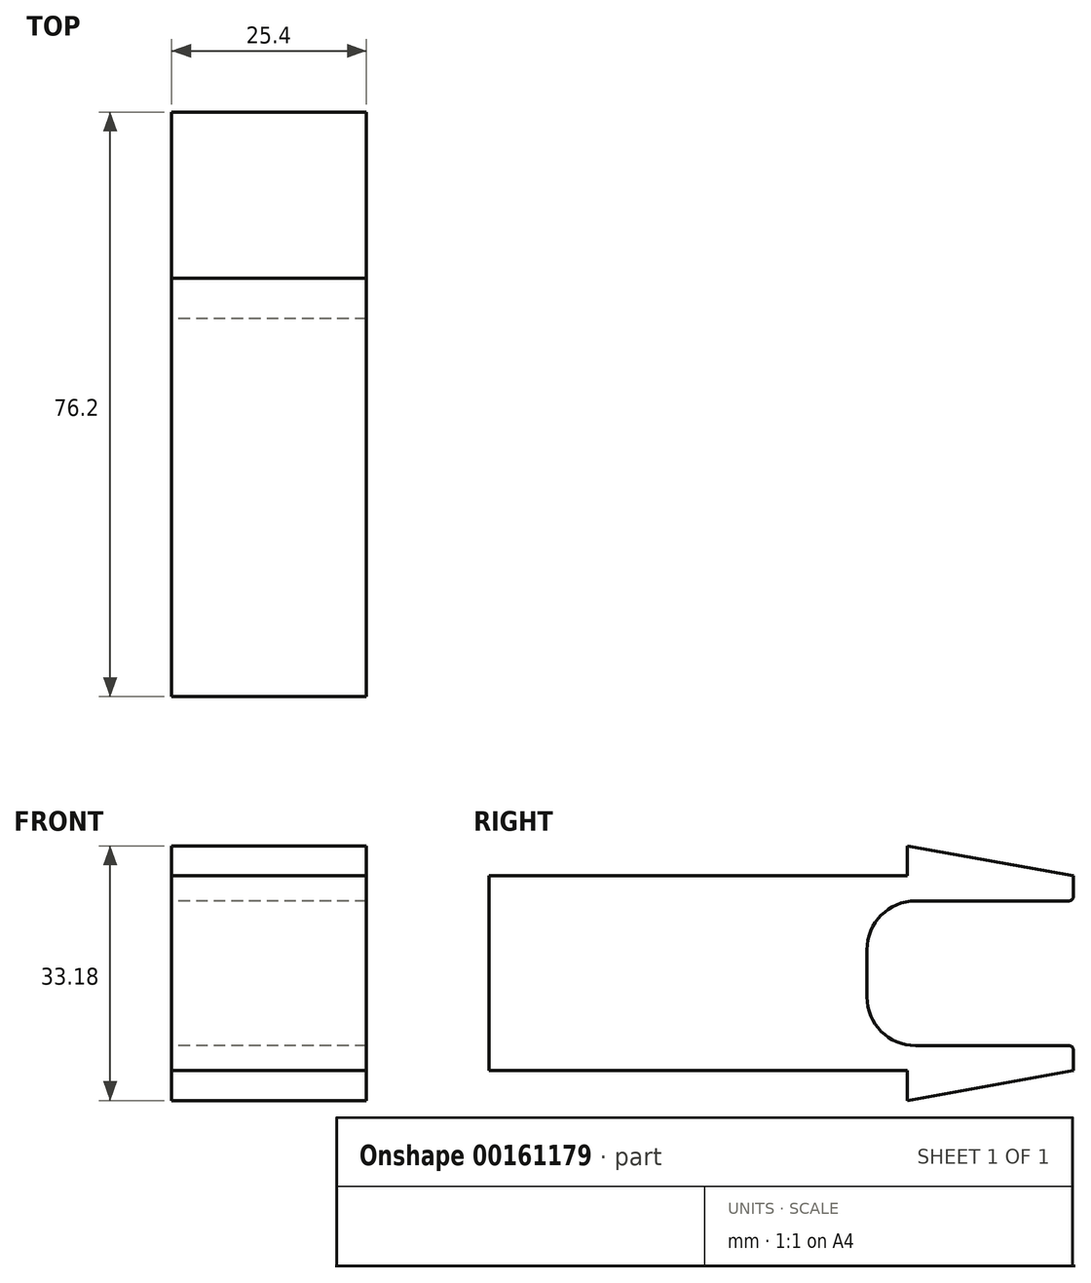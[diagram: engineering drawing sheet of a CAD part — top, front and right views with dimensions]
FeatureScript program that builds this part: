
annotation { "Feature Type Name" : "Feature", "Feature Type Description" : "" }
export const myFeature = defineFeature(function(context is Context, id is Id, definition is map)
    precondition{}
    {
        {
            var Q0;
            Q0=qCreatedBy(makeId("Right.planeOp"),FACE);
            var sketch = newSketch(context, id + "F0", { "sketchPlane" : qUnion([Q0])});
            skLineSegment(sketch, "E0.bottom", {"start": v(-38.1, 12.7) * mm, "end": v(38.1, 12.7) * mm});
            skLineSegment(sketch, "E0.top", {"start": v(-38.1, -12.7) * mm, "end": v(38.1, -12.7) * mm});
            skLineSegment(sketch, "E0.left", {"start": v(-38.1, 12.7) * mm, "end": v(-38.1, -12.7) * mm});
            skLineSegment(sketch, "E0.right", {"start": v(38.1, 12.7) * mm, "end": v(38.1, 10.06) * mm});
            skPoint(sketch, "E1", {"position": v(0, 12.7) * mm});
            skPoint(sketch, "E2", {"position": v(0, -12.7) * mm});
            skPoint(sketch, "E3", {"position": v(38.1, 0) * mm});
            skPoint(sketch, "E3.positionSnap0", {"position": v(38.1, 0) * mm});
            skPoint(sketch, "E4", {"position": v(-38.1, 0) * mm});
            skLineSegment(sketch, "E5", {"start": v(16.45, 12.7) * mm, "end": v(16.45, 16.59) * mm});
            skLineSegment(sketch, "E6", {"start": v(16.45, 16.59) * mm, "end": v(38.1, 12.7) * mm});
            skLineSegment(sketch, "E7", {"start": v(16.45, -12.7) * mm, "end": v(16.45, -16.59) * mm});
            skLineSegment(sketch, "E8", {"start": v(16.45, -16.59) * mm, "end": v(38.1, -12.7) * mm});
            skLineSegment(sketch, "E9.bottom", {"start": v(17.52, 9.43) * mm, "end": v(37.46, 9.43) * mm});
            skLineSegment(sketch, "E9.top", {"start": v(17.52, -9.43) * mm, "end": v(37.46, -9.43) * mm});
            skLineSegment(sketch, "E9.left", {"start": v(11.17, 3.08) * mm, "end": v(11.17, -3.08) * mm});
            skLineSegment(sketch, "E9.right", {"start": v(38.1, 9.43) * mm, "end": v(38.1, -9.43) * mm});
            skPoint(sketch, "E10", {"position": v(11.17, 0) * mm});
            skPoint(sketch, "E11.visualSharp", {"position": v(11.17, 9.43) * mm});
            skArc(sketch, "E11.filletArc", {"start": v(17.52, 9.43) * mm, "mid": v(13.03, 7.57) * mm, "end": v(11.17, 3.08) * mm});
            skPoint(sketch, "E12.visualSharp", {"position": v(11.17, -9.43) * mm});
            skArc(sketch, "E12.filletArc", {"start": v(11.17, -3.08) * mm, "mid": v(13.03, -7.57) * mm, "end": v(17.52, -9.43) * mm});
            skPoint(sketch, "E13.newPointB", {"position": v(38.1, -12.7) * mm});
            skArc(sketch, "E13.filletArc", {"start": v(37.46, 9.43) * mm, "mid": v(37.91, 9.61) * mm, "end": v(38.1, 10.06) * mm});
            skLineSegment(sketch, "E14", {"start": v(38.1, -12.7) * mm, "end": v(38.1, -10.06) * mm});
            skPoint(sketch, "E15.visualSharp", {"position": v(38.1, -9.43) * mm});
            skArc(sketch, "E15.filletArc", {"start": v(38.1, -10.06) * mm, "mid": v(37.91, -9.61) * mm, "end": v(37.46, -9.43) * mm});
            skSolve(sketch);
        }
        {
            var Q0;
            {var subQ4=sQuery(id+"F0.wireOp",EDGE,"E0.left");Q0=makeQuery(id+"F0.imprint","IMPRINT",FACE,{"disambiguationData":[TD([[makeQuery(id+"F0.imprint","IMPRINT",EDGE,{"derivedFrom":subQ4}),1.0]])]});}
            var Q1;
            {var subQ2=sQuery(id+"F0.wireOp",EDGE,"E5");Q1=makeQuery(id+"F0.imprint","IMPRINT",FACE,{"disambiguationData":[TD([[makeQuery(id+"F0.imprint","IMPRINT",EDGE,{"derivedFrom":subQ2}),-1.0]])]});}
            var Q2;
            {var subQ2=sQuery(id+"F0.wireOp",EDGE,"E7");Q2=makeQuery(id+"F0.imprint","IMPRINT",FACE,{"disambiguationData":[TD([[makeQuery(id+"F0.imprint","IMPRINT",EDGE,{"derivedFrom":subQ2}),1.0]])]});}
            extrude(context, id + "F1", {"entities" : qUnion([Q0, Q1, Q2]), "depth" : 25.4 * mm});
        }
    });
